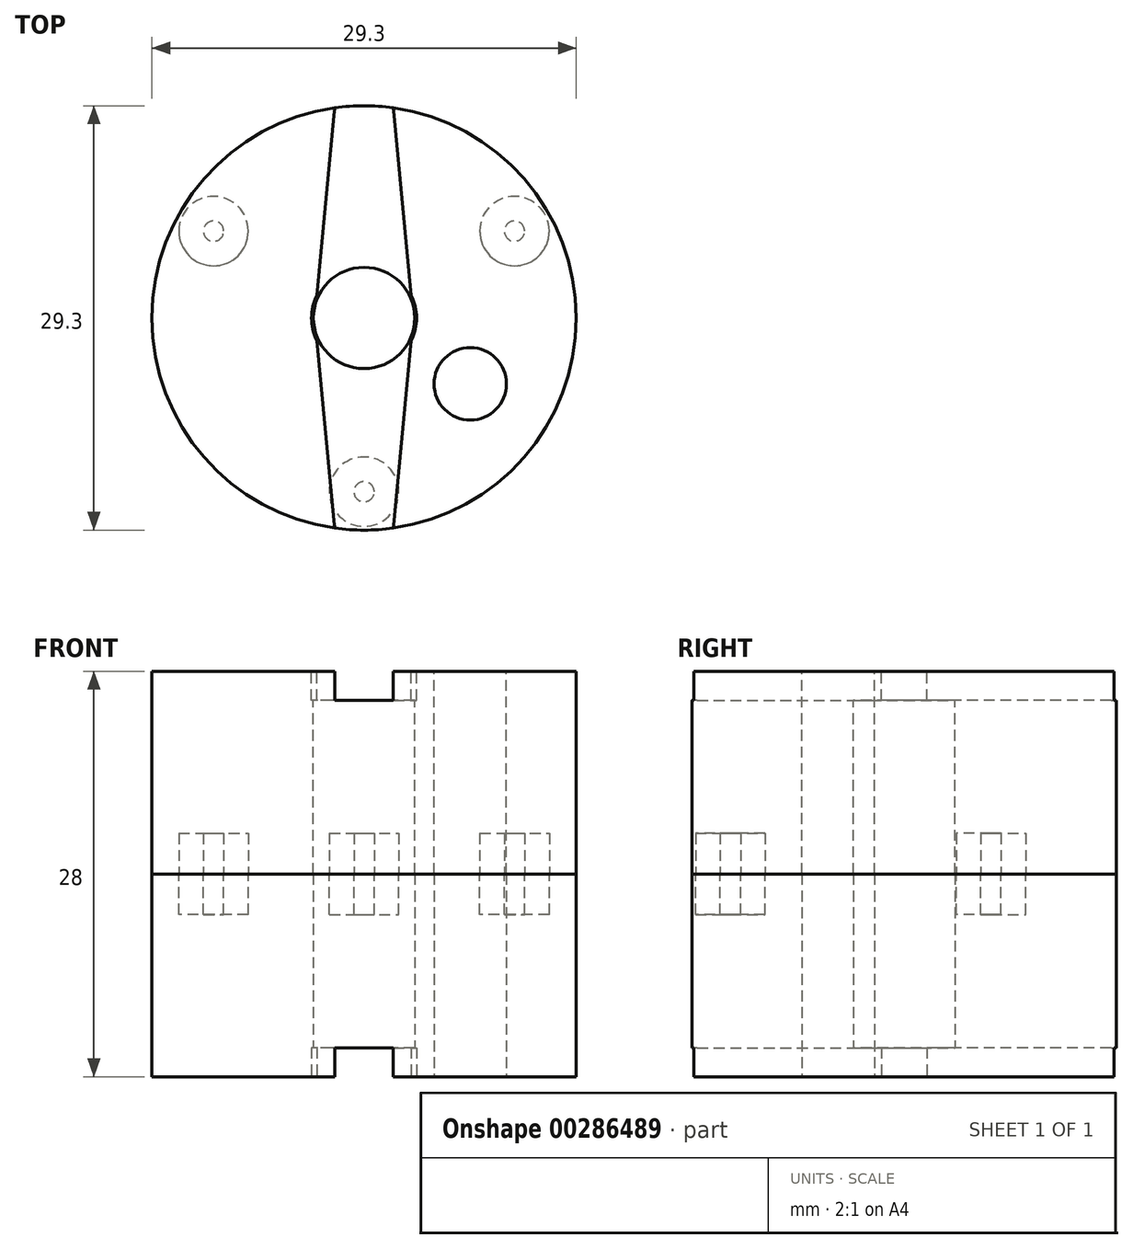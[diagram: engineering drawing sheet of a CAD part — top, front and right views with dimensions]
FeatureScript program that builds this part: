
annotation { "Feature Type Name" : "Feature", "Feature Type Description" : "" }
export const myFeature = defineFeature(function(context is Context, id is Id, definition is map)
    precondition{}
    {
        {
            var Q0;
            Q0=qCreatedBy(makeId("Top.planeOp"),FACE);
            var sketch = newSketch(context, id + "F0", { "sketchPlane" : qUnion([Q0])});
            skCircle(sketch, "E0", {"center": v(0, 0) * mm, "radius": 14.65 * mm});
            skSolve(sketch);
        }
        {
            var Q0;
            Q0 = qSketchRegion(id + "F0", true);
            extrude(context, id + "F1", {"entities" : qUnion([Q0]), "depth" : 14 * mm, "offsetDistance" : 25 * mm});
        }
        {
            var Q0;
            Q0=makeQuery(id+"F1.opExtrude","CAP_FACE",FACE,{"disambiguationData":[OSD([sQuery(id+"F0.wireOp",EDGE,"E0")])],"isStart":true});
            var sketch = newSketch(context, id + "F2", { "sketchPlane" : qUnion([Q0])});
            skCircle(sketch, "E1", {"center": v(0, 12) * mm, "radius": 2.4 * mm});
            skCircle(sketch, "E2", {"center": v(0, 12) * mm, "radius": 0.7 * mm});
            skCircle(sketch, "E3.1.0", {"center": v(-10.4, -6) * mm, "radius": 2.4 * mm});
            skCircle(sketch, "E3.1.1", {"center": v(-10.4, -6) * mm, "radius": 0.7 * mm});
            skCircle(sketch, "E3.2.0", {"center": v(10.4, -6) * mm, "radius": 2.4 * mm});
            skCircle(sketch, "E3.2.1", {"center": v(10.4, -6) * mm, "radius": 0.7 * mm});
            skPoint(sketch, "E3.center", {"position": v(0, 0) * mm});
            skLineSegment(sketch, "E4", {"start": v(-10.4, -8.4) * mm, "end": v(10.4, -8.4) * mm, "construction": true});
            skSolve(sketch);
        }
        {
            var Q0;
            Q0 = qSketchRegion(id + "F2", true);
            extrude(context, id + "F3", {"entities" : qUnion([Q0]), "operationType" : NewBodyOperationType.ADD, "depth" : 2.8 * mm, "offsetDistance" : 25 * mm});
        }
        {
            var Q0;
            Q0=makeQuery(id+"F1.opExtrude","CAP_FACE",FACE,{"disambiguationData":[OSD([sQuery(id+"F0.wireOp",EDGE,"E0")])],"isStart":false});
            var sketch = newSketch(context, id + "F4", { "sketchPlane" : qUnion([Q0])});
            skCircle(sketch, "E5", {"center": v(0, 0) * mm, "radius": 3.5 * mm});
            skCircle(sketch, "E6", {"center": v(7.34, -4.55) * mm, "radius": 2.5 * mm});
            skSolve(sketch);
        }
        {
            var Q0;
            Q0 = qSketchRegion(id + "F4", true);
            extrude(context, id + "F5", {"entities" : qUnion([Q0]), "operationType" : NewBodyOperationType.REMOVE, "oppositeDirection" : true, "depth" : 25 * mm, "offsetDistance" : 25 * mm});
        }
        {
            var Q0;
            Q0=makeQuery(id+"F1.opExtrude","CAP_FACE",FACE,{"disambiguationData":[OSD([sQuery(id+"F0.wireOp",EDGE,"E0")])],"isStart":false});
            var sketch = newSketch(context, id + "F6", { "sketchPlane" : qUnion([Q0])});
            skCircle(sketch, "E7", {"center": v(0, 0) * mm, "radius": 3.62 * mm});
            skCircle(sketch, "E8", {"center": v(0, 14.1) * mm, "radius": 2.05 * mm});
            skCircle(sketch, "E9.MirrorC", {"center": v(0, -14.1) * mm, "radius": 2.05 * mm});
            skLineSegment(sketch, "E10", {"start": v(-2.04, 14.3) * mm, "end": v(-3.3, 1.15) * mm});
            skLineSegment(sketch, "E11.MirrorCS", {"start": v(2.04, 14.3) * mm, "end": v(3.3, 1.15) * mm});
            skLineSegment(sketch, "E12.MirrorCS", {"start": v(-2.04, -14.3) * mm, "end": v(-3.3, -1.15) * mm});
            skLineSegment(sketch, "E13.MirrorCS", {"start": v(2.04, -14.3) * mm, "end": v(3.3, -1.15) * mm});
            skSolve(sketch);
        }
        {
            var Q0;
            Q0 = qSketchRegion(id + "F6", true);
            extrude(context, id + "F7", {"entities" : qUnion([Q0]), "operationType" : NewBodyOperationType.REMOVE, "oppositeDirection" : true, "depth" : 2 * mm, "offsetDistance" : 25 * mm});
        }
        {
            var Q0;
            Q0=makeQuery(id+"F1.opExtrude","SWEPT_BODY",BODY,{"disambiguationData":[OSD([sQuery(id+"F0.wireOp",EDGE,"E0")])]});
            var Q1;
            Q1=qCreatedBy(makeId("Top.planeOp"),FACE);
            mirror(context, id + "F8", {"entities" : qUnion([Q0]), "mirrorPlane" : qUnion([Q1])});
        }
    });
